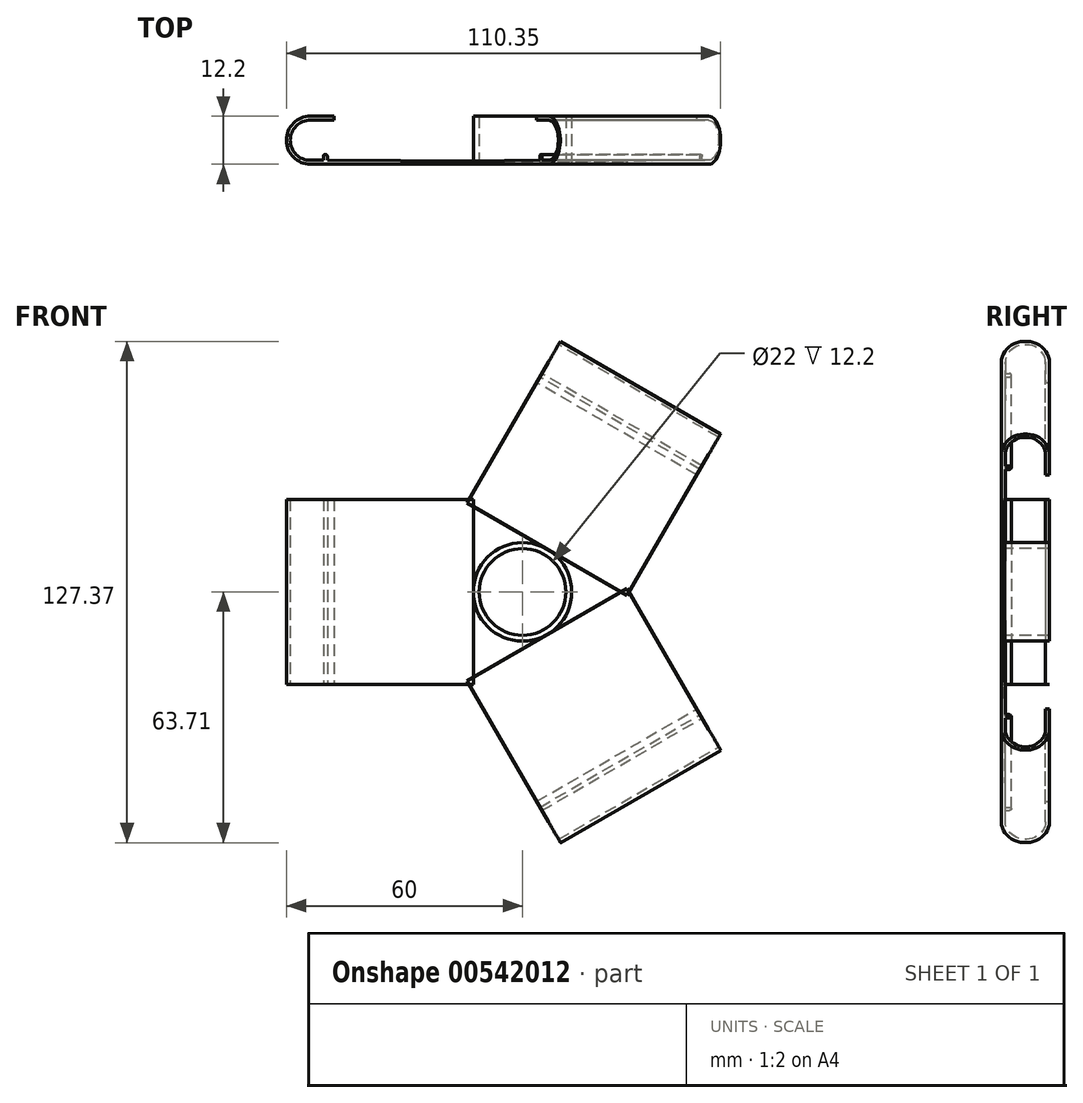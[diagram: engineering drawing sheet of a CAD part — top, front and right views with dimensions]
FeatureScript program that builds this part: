
annotation { "Feature Type Name" : "Feature", "Feature Type Description" : "" }
export const myFeature = defineFeature(function(context is Context, id is Id, definition is map)
    precondition{}
    {
        {
            var Q0;
            Q0=qCreatedBy(makeId("Front.planeOp"),FACE);
            var sketch = newSketch(context, id + "F0", { "sketchPlane" : qUnion([Q0])});
            skCircle(sketch, "E0", {"center": v(0, 0) * mm, "radius": 11 * mm});
            skCircle(sketch, "E1", {"center": v(0, 0) * mm, "radius": 12.5 * mm});
            skLineSegment(sketch, "E2.0", {"start": v(0, 69.28) * mm, "end": v(60, 34.64) * mm});
            skLineSegment(sketch, "E2.2", {"start": v(60, -34.64) * mm, "end": v(0, -69.28) * mm});
            skLineSegment(sketch, "E2.4", {"start": v(-60, -34.64) * mm, "end": v(-60, 34.64) * mm});
            skLineSegment(sketch, "E3", {"start": v(0, 12.5) * mm, "end": v(0, 69.28) * mm, "construction": true});
            skLineSegment(sketch, "E4", {"start": v(-10.83, 6.25) * mm, "end": v(-60, 34.64) * mm, "construction": true});
            skLineSegment(sketch, "E5", {"start": v(-12.5, 0) * mm, "end": v(-69.28, 0) * mm, "construction": true});
            skLineSegment(sketch, "E6", {"start": v(-69.28, 0) * mm, "end": v(-12.5, 0) * mm, "construction": true});
            skLineSegment(sketch, "E7", {"start": v(0, -69.28) * mm, "end": v(0, -12.5) * mm, "construction": true});
            skLineSegment(sketch, "E8", {"start": v(-6.25, -10.83) * mm, "end": v(-34.64, -60) * mm, "construction": true});
            skLineSegment(sketch, "E9", {"start": v(12.5, 0) * mm, "end": v(69.28, 0) * mm, "construction": true});
            skLineSegment(sketch, "E10", {"start": v(6.25, 10.83) * mm, "end": v(34.64, 60) * mm, "construction": true});
            skLineSegment(sketch, "E11", {"start": v(10.83, -6.25) * mm, "end": v(60, -34.64) * mm, "construction": true});
            skLineSegment(sketch, "E12", {"start": v(-10.83, -6.25) * mm, "end": v(-60, -34.64) * mm, "construction": true});
            skLineSegment(sketch, "E13", {"start": v(-6.25, 10.83) * mm, "end": v(-34.64, 60) * mm, "construction": true});
            skLineSegment(sketch, "E14", {"start": v(10.83, 6.25) * mm, "end": v(60, 34.64) * mm, "construction": true});
            skLineSegment(sketch, "E15", {"start": v(6.25, -10.83) * mm, "end": v(34.64, -60) * mm, "construction": true});
            skSolve(sketch);
        }
        {
            var Q0;
            Q0=makeQuery(id+"F0.imprint","IMPRINT",FACE,{"disambiguationData":[TD([[makeQuery(id+"F0.imprint","IMPRINT",EDGE,{"derivedFrom":sQuery(id+"F0.wireOp",EDGE,"E0")}),-1.0]])]});
            extrude(context, id + "F1", {"entities" : qUnion([Q0]), "oppositeDirection" : true, "depth" : 12.2 * mm, "offsetDistance" : 25 * mm});
        }
        {
            var Q0;
            Q0=qCreatedBy(makeId("Top.planeOp"),FACE);
            var sketch = newSketch(context, id + "F2", { "sketchPlane" : qUnion([Q0])});
            skArc(sketch, "E16", {"start": v(-53.9, 11.2) * mm, "mid": v(-59, 6.1) * mm, "end": v(-53.9, 1) * mm});
            skArc(sketch, "E17", {"start": v(-53.9, 12.2) * mm, "mid": v(-60, 6.1) * mm, "end": v(-53.9, 0) * mm});
            skLineSegment(sketch, "E18", {"start": v(-53.9, 6.1) * mm, "end": v(-53.9, 11.2) * mm, "construction": true});
            skLineSegment(sketch, "E19", {"start": v(-53.9, 6.1) * mm, "end": v(-53.9, 1) * mm, "construction": true});
            skLineSegment(sketch, "E20", {"start": v(-53.9, 0) * mm, "end": v(-49.58, 0) * mm});
            skLineSegment(sketch, "E21", {"start": v(-53.9, 1) * mm, "end": v(-50.58, 1) * mm});
            skPoint(sketch, "E22", {"position": v(-50.58, 1) * mm});
            skLineSegment(sketch, "E23.left", {"start": v(-50.58, 1) * mm, "end": v(-50.58, 2) * mm});
            skLineSegment(sketch, "E23.right", {"start": v(-49.58, 1) * mm, "end": v(-49.58, 2) * mm});
            skCircle(sketch, "E24", {"center": v(-53.9, 6.1) * mm, "radius": 5.08 * mm, "construction": true});
            skArc(sketch, "E25", {"start": v(-49.58, 2) * mm, "mid": v(-50.08, 2.5) * mm, "end": v(-50.58, 2) * mm});
            skLineSegment(sketch, "E26", {"start": v(0, 0.72) * mm, "end": v(0, 26.09) * mm, "construction": true});
            skLineSegment(sketch, "E27", {"start": v(-12.5, 0) * mm, "end": v(-53.9, 0) * mm, "construction": true});
            skLineSegment(sketch, "E28", {"start": v(0, 0) * mm, "end": v(0, -37.62) * mm, "construction": true});
            skPoint(sketch, "E29", {"position": v(-49.58, 1) * mm});
            skPoint(sketch, "E30", {"position": v(-49.58, 0) * mm});
            skLineSegment(sketch, "E31", {"start": v(0, 0) * mm, "end": v(-49.58, 0) * mm});
            skLineSegment(sketch, "E32", {"start": v(-49.58, 1) * mm, "end": v(-12.5, 0.79) * mm});
            skLineSegment(sketch, "E33", {"start": v(0, 0.72) * mm, "end": v(0, 0) * mm});
            skLineSegment(sketch, "E34", {"start": v(-53.9, 11.2) * mm, "end": v(-47.9, 11.2) * mm});
            skLineSegment(sketch, "E35", {"start": v(-47.9, 11.2) * mm, "end": v(-47.9, 12.2) * mm});
            skLineSegment(sketch, "E36", {"start": v(-47.9, 12.2) * mm, "end": v(-53.9, 12.2) * mm});
            skPoint(sketch, "E37.start.orphan", {"position": v(-60, 6.1) * mm});
            skLineSegment(sketch, "E38.0", {"start": v(12.5, 0) * mm, "end": v(-12.5, 0) * mm});
            skLineSegment(sketch, "E39", {"start": v(-53.9, 0) * mm, "end": v(-12.5, 0) * mm});
            skPoint(sketch, "E40", {"position": v(-12.5, 0.79) * mm});
            skPoint(sketch, "E41", {"position": v(-12.5, 0) * mm});
            skLineSegment(sketch, "E42", {"start": v(-12.5, 0) * mm, "end": v(-12.5, 0.79) * mm});
            skSolve(sketch);
        }
        {
            var Q0;
            Q0=makeQuery(id+"F2.imprint","IMPRINT",FACE,{"disambiguationData":[TD([[makeQuery(id+"F2.imprint","IMPRINT",EDGE,{"derivedFrom":sQuery(id+"F2.wireOp",EDGE,"E16")}),-1.0]])]});
            extrude(context, id + "F3", {"entities" : qUnion([Q0]), "endBound" : BoundingType.SYMMETRIC, "depth" : 47 * mm, "offsetDistance" : 25 * mm});
        }
        {
            var Q0;
            Q0=sQuery(id+"F0.wireOp",EDGE,"E2.2");
            cPoint(context, id + "F4", {"entities" : qUnion([Q0]), "parameter" : 0.5});
        }
        {
            var Q0;
            Q0=sQuery(id+"F0.wireOp",EDGE,"E2.2");
            var Q1;
            Q1 = qCreatedBy(id + "F4" ,VERTEX);
            cPlane(context, id + "F5", {"entities" : qUnion([Q0, Q1]), "cplaneType" : CPlaneType.LINE_POINT, "offset" : 25 * mm, "width" : 150 * mm, "height" : 150 * mm});
        }
        {
            var Q0;
            Q0=qCreatedBy(id+"F5.planeOp",FACE);
            var sketch = newSketch(context, id + "F6", { "sketchPlane" : qUnion([Q0])});
            skArc(sketch, "E43", {"start": v(-11.2, -53.9) * mm, "mid": v(-6.1, -59) * mm, "end": v(-1, -53.9) * mm});
            skArc(sketch, "E44", {"start": v(-12.2, -53.9) * mm, "mid": v(-6.1, -60) * mm, "end": v(0, -53.9) * mm});
            skLineSegment(sketch, "E45", {"start": v(-6.1, -53.9) * mm, "end": v(-11.2, -53.9) * mm, "construction": true});
            skLineSegment(sketch, "E46", {"start": v(-6.1, -53.9) * mm, "end": v(-1, -53.9) * mm, "construction": true});
            skLineSegment(sketch, "E47", {"start": v(0, -53.9) * mm, "end": v(0, -49.58) * mm});
            skLineSegment(sketch, "E48", {"start": v(-1, -53.9) * mm, "end": v(-1, -50.58) * mm});
            skPoint(sketch, "E49", {"position": v(-1, -50.58) * mm});
            skLineSegment(sketch, "E50.left", {"start": v(-1, -50.58) * mm, "end": v(-2, -50.58) * mm});
            skLineSegment(sketch, "E50.right", {"start": v(-1, -49.58) * mm, "end": v(-2, -49.58) * mm});
            skCircle(sketch, "E51", {"center": v(-6.1, -53.9) * mm, "radius": 5.08 * mm, "construction": true});
            skArc(sketch, "E52", {"start": v(-2, -49.58) * mm, "mid": v(-2.5, -50.08) * mm, "end": v(-2, -50.58) * mm});
            skLineSegment(sketch, "E53", {"start": v(0, -12.5) * mm, "end": v(0, -53.9) * mm, "construction": true});
            skPoint(sketch, "E54", {"position": v(-1, -49.58) * mm});
            skPoint(sketch, "E55", {"position": v(0, -49.58) * mm});
            skLineSegment(sketch, "E56", {"start": v(0, 0) * mm, "end": v(0, -49.58) * mm});
            skLineSegment(sketch, "E57", {"start": v(-1, -49.58) * mm, "end": v(-0.79, -12.5) * mm});
            skLineSegment(sketch, "E58", {"start": v(-11.2, -53.9) * mm, "end": v(-11.2, -47.9) * mm});
            skLineSegment(sketch, "E59", {"start": v(-11.2, -47.9) * mm, "end": v(-12.2, -47.9) * mm});
            skLineSegment(sketch, "E60", {"start": v(-12.2, -47.9) * mm, "end": v(-12.2, -53.9) * mm});
            skPoint(sketch, "E61.start.orphan", {"position": v(-6.1, -60) * mm});
            skLineSegment(sketch, "E62", {"start": v(-0.79, -12.5) * mm, "end": v(0, -12.5) * mm});
            skSolve(sketch);
        }
        {
            var Q0;
            Q0=makeQuery(id+"F6.imprint","IMPRINT",FACE,{"disambiguationData":[TD([[makeQuery(id+"F6.imprint","IMPRINT",EDGE,{"derivedFrom":sQuery(id+"F6.wireOp",EDGE,"E43")}),-1.0]])]});
            extrude(context, id + "F7", {"entities" : qUnion([Q0]), "endBound" : BoundingType.SYMMETRIC, "depth" : 47 * mm, "offsetDistance" : 25 * mm});
        }
        {
            var Q0;
            Q0=sQuery(id+"F0.wireOp",EDGE,"E2.0");
            cPoint(context, id + "F8", {"entities" : qUnion([Q0]), "parameter" : 0.5});
        }
        {
            var Q0;
            Q0=sQuery(id+"F0.wireOp",EDGE,"E2.0");
            var Q1;
            Q1 = qCreatedBy(id + "F8" ,VERTEX);
            cPlane(context, id + "F9", {"entities" : qUnion([Q0, Q1]), "cplaneType" : CPlaneType.LINE_POINT, "offset" : 25 * mm, "width" : 150 * mm, "height" : 150 * mm});
        }
        {
            var Q0;
            Q0=qCreatedBy(id+"F9.planeOp",FACE);
            var sketch = newSketch(context, id + "F10", { "sketchPlane" : qUnion([Q0])});
            skArc(sketch, "E63", {"start": v(11.2, 53.85) * mm, "mid": v(6.1, 58.95) * mm, "end": v(1, 53.85) * mm});
            skArc(sketch, "E64", {"start": v(12.2, 53.85) * mm, "mid": v(6.1, 59.95) * mm, "end": v(0, 53.85) * mm});
            skLineSegment(sketch, "E65", {"start": v(6.1, 53.85) * mm, "end": v(11.2, 53.85) * mm, "construction": true});
            skLineSegment(sketch, "E66", {"start": v(6.1, 53.85) * mm, "end": v(1, 53.85) * mm, "construction": true});
            skLineSegment(sketch, "E67", {"start": v(0, 53.85) * mm, "end": v(0, 49.53) * mm});
            skLineSegment(sketch, "E68", {"start": v(1, 53.85) * mm, "end": v(1, 50.53) * mm});
            skPoint(sketch, "E69", {"position": v(1, 50.53) * mm});
            skLineSegment(sketch, "E70.left", {"start": v(1, 50.53) * mm, "end": v(2, 50.53) * mm});
            skLineSegment(sketch, "E70.right", {"start": v(1, 49.53) * mm, "end": v(2, 49.53) * mm});
            skCircle(sketch, "E71", {"center": v(6.1, 53.85) * mm, "radius": 5.08 * mm, "construction": true});
            skArc(sketch, "E72", {"start": v(2, 49.53) * mm, "mid": v(2.5, 50.03) * mm, "end": v(2, 50.53) * mm});
            skLineSegment(sketch, "E73", {"start": v(0, 12.5) * mm, "end": v(0, 53.85) * mm, "construction": true});
            skPoint(sketch, "E74", {"position": v(1, 49.53) * mm});
            skPoint(sketch, "E75", {"position": v(0, 49.53) * mm});
            skLineSegment(sketch, "E76", {"start": v(0, -0.05) * mm, "end": v(0, 49.53) * mm});
            skLineSegment(sketch, "E77", {"start": v(1, 49.53) * mm, "end": v(0.79, 12.5) * mm});
            skLineSegment(sketch, "E78", {"start": v(11.2, 53.85) * mm, "end": v(11.2, 47.85) * mm});
            skLineSegment(sketch, "E79", {"start": v(11.2, 47.85) * mm, "end": v(12.2, 47.85) * mm});
            skLineSegment(sketch, "E80", {"start": v(12.2, 47.85) * mm, "end": v(12.2, 53.85) * mm});
            skPoint(sketch, "E81.start.orphan", {"position": v(6.1, 59.95) * mm});
            skLineSegment(sketch, "E82.0", {"start": v(0, -12.5) * mm, "end": v(0, 12.5) * mm});
            skLineSegment(sketch, "E83", {"start": v(0, 12.5) * mm, "end": v(0.79, 12.5) * mm});
            skSolve(sketch);
        }
        {
            var Q0;
            Q0=makeQuery(id+"F10.imprint","IMPRINT",FACE,{"disambiguationData":[TD([[makeQuery(id+"F10.imprint","IMPRINT",EDGE,{"derivedFrom":sQuery(id+"F10.wireOp",EDGE,"E63")}),-1.0]])]});
            extrude(context, id + "F11", {"entities" : qUnion([Q0]), "endBound" : BoundingType.SYMMETRIC, "depth" : 47 * mm, "offsetDistance" : 25 * mm});
        }
        {
            var Q0;
            Q0=qCreatedBy(makeId("Front.planeOp"),FACE);
            cPlane(context, id + "F12", {"entities" : qUnion([Q0]), "cplaneType" : CPlaneType.OFFSET, "offset" : 12.2 * mm, "oppositeDirection" : true, "width" : 150 * mm, "height" : 150 * mm});
        }
        {
            var Q0;
            Q0=qCreatedBy(id+"F12.planeOp",FACE);
            var sketch = newSketch(context, id + "F13", { "sketchPlane" : qUnion([Q0])});
            skCircle(sketch, "E84.0", {"center": v(0, 0) * mm, "radius": 11 * mm});
            skSolve(sketch);
        }
        {
            var Q0;
            Q0=makeQuery(id+"F13.imprint","IMPRINT",FACE,{"disambiguationData":[TD([[makeQuery(id+"F13.imprint","IMPRINT",EDGE,{"derivedFrom":sQuery(id+"F13.wireOp",EDGE,"E84.0")}),1.0]])]});
            extrude(context, id + "F14", {"entities" : qUnion([Q0]), "operationType" : NewBodyOperationType.REMOVE, "depth" : 25 * mm, "offsetDistance" : 25 * mm});
        }
    });
